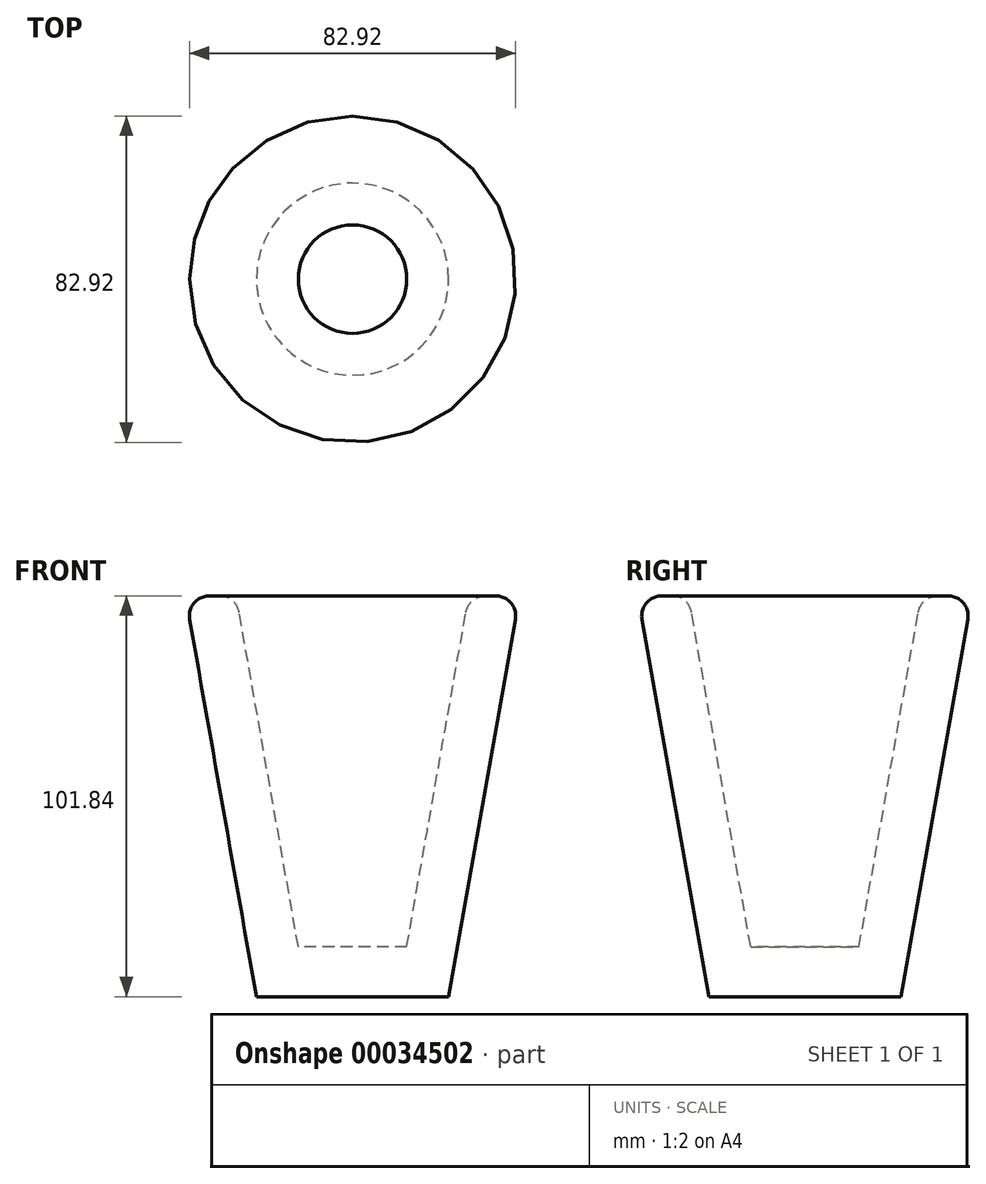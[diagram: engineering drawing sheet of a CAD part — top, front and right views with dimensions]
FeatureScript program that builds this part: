
annotation { "Feature Type Name" : "Feature", "Feature Type Description" : "" }
export const myFeature = defineFeature(function(context is Context, id is Id, definition is map)
    precondition{}
    {
        {
            var Q0;
            Q0=qCreatedBy(makeId("Front.planeOp"),FACE);
            var sketch = newSketch(context, id + "F2", { "sketchPlane" : qUnion([Q0])});
            skLineSegment(sketch, "E0", {"start": v(0, 50.6) * mm, "end": v(42.44, 50.6) * mm});
            skLineSegment(sketch, "E1", {"start": v(42.44, 50.6) * mm, "end": v(24.42, -51.24) * mm});
            skLineSegment(sketch, "E2", {"start": v(24.42, -51.24) * mm, "end": v(0, -51.24) * mm});
            skLineSegment(sketch, "E3", {"start": v(0, -51.24) * mm, "end": v(0, 50.6) * mm});
            skSolve(sketch);
        }
        {
            var Q0;
            Q0=makeQuery(id+"F2.imprint","IMPRINT",FACE,{"disambiguationData":[TD([[makeQuery(id+"F2.imprint","IMPRINT",EDGE,{"derivedFrom":sQuery(id+"F2.wireOp",EDGE,"E0")}),-1.0]])]});
            var Q1;
            Q1=sQuery(id+"F2.wireOp",EDGE,"E0");
            var Q2;
            Q2=sQuery(id+"F2.wireOp",EDGE,"E1");
            var Q3;
            Q3=sQuery(id+"F2.wireOp",EDGE,"E2");
            var Q4;
            Q4=sQuery(id+"F2.wireOp",EDGE,"E3");
            var Q5;
            Q5=sQuery(id+"F2.wireOp",EDGE,"E3");
            revolve(context, id + "F3", {"entities" : qUnion([Q0]), "surfaceEntities" : qUnion([Q1, Q2, Q3, Q4]), "axis" : qUnion([Q5]), "revolveType" : RevolveType.FULL});
        }
        {
            var Q0;
            Q0=makeQuery(id+"F3.opRevolve","SWEPT_FACE",FACE,{"disambiguationData":[OSD([sQuery(id+"F2.wireOp",EDGE,"E0")])]});
            shell(context, id + "F0", {"entities" : qUnion([Q0]), "thickness" : 12.7 * mm});
        }
        {
            var Q0;
            Q0=makeQuery(id+"F3.opRevolve","SWEPT_EDGE",EDGE,{"disambiguationData":[OSD([sQuery(id+"F2.wireOp",EDGE,"E0"),sQuery(id+"F2.wireOp",EDGE,"E1")])]});
            var Q1;
            Q1=makeQuery(id+"F0.opShell","OFFSET_EDGE",EDGE,{"disambiguationData":[OSD([sQuery(id+"F2.wireOp",EDGE,"E0"),sQuery(id+"F2.wireOp",EDGE,"E1")])]});
            fillet(context, id + "F1", {"entities" : qUnion([Q0, Q1]), "radius" : 5.08 * mm, "tangentPropagation" : true, "allowEdgeOverflow" : false});
        }
    });
